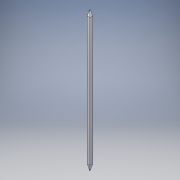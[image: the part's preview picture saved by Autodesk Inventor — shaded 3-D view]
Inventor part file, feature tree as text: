
AUTODESK INVENTOR PART (.ipt)
format: ipt  version: 2018 (Build 220112000, 112)  size: 147,968 bytes
history: native  units: in
note: dims shown in document units (in); Inventor stores cm internally (conversion verified against a paired STEP export)
features: plane x4, sketch x3, extrude x2, loft x1, hole x1, mirror x1, other x1
ambient origin geometry x8: Origin, YZ Plane, XZ Plane, XY Plane, X Axis, Y Axis, Z Axis, Center Point
bodies: Body1 (feature_tree)
feature tree (13):
  extrude  "Extrusion3"  Depth=36.0in
  plane  "Work Plane4"
  loft  "Loft3"
  plane  "Work Plane5"
  extrude  "Extrusion4"  Depth=12.0in
  hole  "Hole1"  [1 undecoded]
  mirror  "Mirror1"
  sketch  "Sketch5"  dims[d26=36.0in d27=36.0in]
  sketch  "Sketch6"  dims[d28=1716.0in d29=0.0in d30=60.0in]
  other  "Edges3"
  sketch  "Sketch7"  dims[d31=12.0in d32=12.0in d33=12.0in d34=12.0in d35=0.0in d36=90.0deg d37=0.0in d38=90.0deg d39=90.0deg d40=12.0in d41=1320.0in d42=0.0in d43=1.0in d44=1.0in d45=3.0in d46=0.75in d47=0.375in d48=0.25in d49=0.5635in d50=1.0in d51=0.8108in]
  plane  "Work Plane6"
  plane  "Work Plane7"
note: 1 required parameter value undecoded (feature->parameter linkage not recoverable at this tier; creation-order binding heuristic only, values carry confidence <= 0.55)
